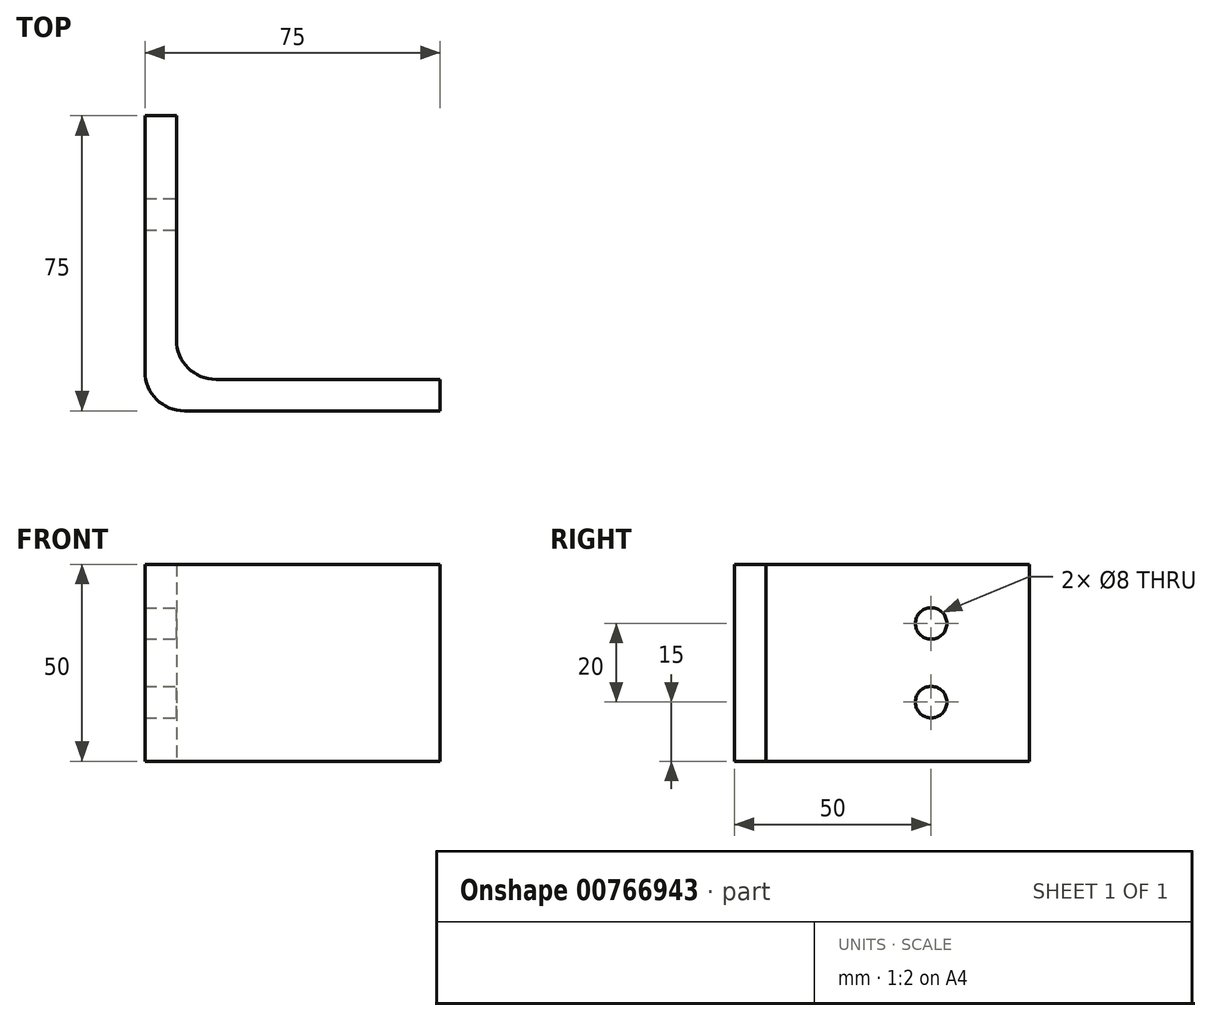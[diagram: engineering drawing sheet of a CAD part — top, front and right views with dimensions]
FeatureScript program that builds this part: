
annotation { "Feature Type Name" : "Feature", "Feature Type Description" : "" }
export const myFeature = defineFeature(function(context is Context, id is Id, definition is map)
    precondition{}
    {
        {
            var Q0;
            Q0=qCreatedBy(makeId("Top.planeOp"),FACE);
            var sketch = newSketch(context, id + "F0", { "sketchPlane" : qUnion([Q0])});
            skLineSegment(sketch, "E0.top", {"start": v(0, 75) * mm, "end": v(8, 75) * mm});
            skLineSegment(sketch, "E0.left", {"start": v(0, 0) * mm, "end": v(0, 75) * mm});
            skLineSegment(sketch, "E1", {"start": v(8, 8) * mm, "end": v(75, 8) * mm});
            skLineSegment(sketch, "E2", {"start": v(0, 0) * mm, "end": v(75, 0) * mm});
            skLineSegment(sketch, "E3", {"start": v(75, 0) * mm, "end": v(75, 8) * mm});
            skLineSegment(sketch, "E4", {"start": v(8, 8) * mm, "end": v(8, 75) * mm});
            skSolve(sketch);
        }
        {
            var Q0;
            Q0 = qSketchRegion(id + "F0", true);
            extrude(context, id + "F1", {"entities" : qUnion([Q0]), "depth" : 50 * mm, "offsetDistance" : 25 * mm});
        }
        {
            var Q0;
            Q0=makeQuery(id+"F1.opExtrude","SWEPT_EDGE",EDGE,{"disambiguationData":[OSD([sQuery(id+"F0.wireOp",EDGE,"E1"),sQuery(id+"F0.wireOp",EDGE,"E4")])]});
            var Q1;
            Q1=makeQuery(id+"F1.opExtrude","SWEPT_EDGE",EDGE,{"disambiguationData":[OSD([sQuery(id+"F0.wireOp",EDGE,"E0.left"),sQuery(id+"F0.wireOp",EDGE,"E2")])]});
            fillet(context, id + "F2", {"entities" : qUnion([Q0, Q1]), "radius" : 10 * mm, "tangentPropagation" : true, "allowEdgeOverflow" : false});
        }
        {
            var Q0;
            Q0=makeQuery(id+"F1.opExtrude","SWEPT_FACE",FACE,{"disambiguationData":[OSD([sQuery(id+"F0.wireOp",EDGE,"E4")])]});
            var sketch = newSketch(context, id + "F3", { "sketchPlane" : qUnion([Q0])});
            skCircle(sketch, "E5", {"center": v(50, 35) * mm, "radius": 4 * mm});
            skCircle(sketch, "E6", {"center": v(50, 15) * mm, "radius": 4 * mm});
            skSolve(sketch);
        }
        {
            var Q0;
            Q0 = qSketchRegion(id + "F3", true);
            extrude(context, id + "F4", {"entities" : qUnion([Q0]), "operationType" : NewBodyOperationType.REMOVE, "endBound" : BoundingType.THROUGH_ALL, "oppositeDirection" : true, "depth" : 25 * mm, "offsetDistance" : 25 * mm});
        }
    });
